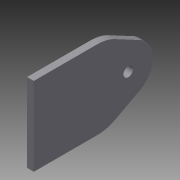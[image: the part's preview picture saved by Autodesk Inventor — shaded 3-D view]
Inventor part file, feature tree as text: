
AUTODESK INVENTOR PART (.ipt)
format: ipt  version: 2015 (Build 190159000, 159)  size: 88,576 bytes
history: native  units: mm
features: extrude x1, sketch x1
ambient origin geometry x8: Origin, YZ Plane, XZ Plane, XY Plane, X Axis, Y Axis, Z Axis, Center Point
bodies: Body1 (feature_tree)
feature tree (2):
  extrude  "Extrusion3"  Depth=6.0mm
  sketch  "Sketch3"  dims[d4=32.0mm d9=50.0mm d27=44.0mm d28=44.0mm d31=8.5mm d32=44.0mm d33=27.64mm d35=12.7mm d41=84.0mm d42=6.0mm d43=0.0mm]
